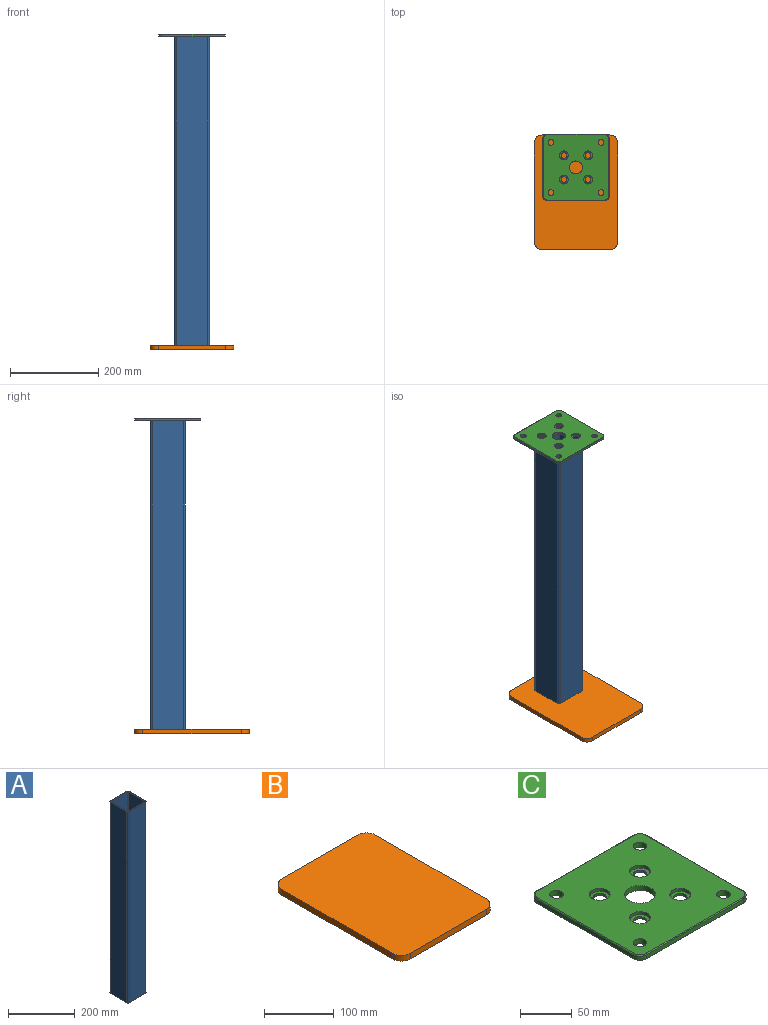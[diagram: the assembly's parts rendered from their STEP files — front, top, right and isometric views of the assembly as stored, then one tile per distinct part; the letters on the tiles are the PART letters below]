
ASSEMBLY  parts=3 mates=2
PART A: 18 faces, bbox 80x80x700 mm
  f0: cylinder r=2mm len=700mm, axis (0,0,-1), area 2199.1mm2, adj f1,f15,f16,f17
  f1: plane 700x70mm, normal (-1,0,0), area 49000mm2, adj f0,f2,f16,f17
  f2: cylinder r=2mm len=700mm, axis (0,0,-1), area 2199.1mm2, adj f1,f3,f16,f17
  f3: plane 700x70mm, normal (0,1,0), area 49000mm2, adj f2,f4,f16,f17
  f4: cylinder r=2mm len=700mm, axis (0,0,-1), area 2199.1mm2, adj f3,f5,f16,f17
  f5: plane 700x70mm, normal (1,0,0), area 49000mm2, adj f4,f6,f16,f17
  f6: cylinder r=2mm len=700mm, axis (0,0,-1), area 2199.1mm2, adj f5,f15,f16,f17
  f7: plane 700x70mm, normal (0,-1,0), area 49000mm2, adj f8,f14,f16,f17
  f8: cylinder r=5mm len=700mm, axis (0,0,-1), area 5497.8mm2, adj f7,f9,f16,f17
  f9: plane 700x70mm, normal (1,0,0), area 49000mm2, adj f8,f10,f16,f17
  f10: cylinder r=5mm len=700mm, axis (0,0,-1), area 5497.8mm2, adj f9,f11,f16,f17
  f11: plane 700x70mm, normal (0,1,0), area 49000mm2, adj f10,f12,f16,f17
  f12: cylinder r=5mm len=700mm, axis (0,0,-1), area 5497.8mm2, adj f11,f13,f16,f17
  f13: plane 700x70mm, normal (-1,0,0), area 49000mm2, adj f12,f14,f16,f17
  f14: cylinder r=5mm len=700mm, axis (0,0,-1), area 5497.8mm2, adj f7,f13,f16,f17
  f15: plane 700x70mm, normal (0,-1,0), area 49000mm2, adj f0,f6,f16,f17
  f16: plane 80x80mm, normal (0,0,1), area 906mm2, adj f0,f1,f2,f3,f4,f5,f6,f7
  f17: plane 80x80mm, normal (0,0,-1), area 906mm2, adj f0,f1,f2,f3,f4,f5,f6,f7
PART B: 10 faces, bbox 190x260x10 mm
  f0: plane 154x10mm, normal (0,-1,0), area 1540mm2, adj f4,f5,f6,f9
  f1: plane 224x10mm, normal (1,0,0), area 2240mm2, adj f4,f5,f6,f7
  f2: plane 154x10mm, normal (0,1,0), area 1540mm2, adj f4,f5,f7,f8
  f3: plane 224x10mm, normal (-1,0,0), area 2240mm2, adj f4,f5,f8,f9
  f4: plane 260x190mm, normal (0,0,1), area 49121.9mm2, adj f0,f1,f2,f3,f6,f7,f8,f9
  f5: plane 260x190mm, normal (0,0,-1), area 49121.9mm2, adj f0,f1,f2,f3,f6,f7,f8,f9
  f6: cylinder r=18mm len=18mm, axis (0,0,-1), area 282.7mm2, adj f0,f1,f4,f5
  f7: cylinder r=18mm len=18mm, axis (0,0,1), area 282.7mm2, adj f1,f2,f4,f5
  f8: cylinder r=18mm len=18mm, axis (0,0,-1), area 282.7mm2, adj f2,f3,f4,f5
  f9: cylinder r=18mm len=18mm, axis (0,0,1), area 282.7mm2, adj f0,f3,f4,f5
PART C: 43 faces, bbox 151.5x151.5x6 mm
  f0: plane 132x4.5mm, normal (-1,0,0), area 594mm2, adj f11,f14,f28,f36
  f1: plane 132x4.5mm, normal (0,-1,0), area 594mm2, adj f11,f12,f32,f37
  f2: plane 132x4.5mm, normal (1,0,0), area 594mm2, adj f12,f13,f33,f41
  f3: cylinder r=14.75mm len=29.5mm, axis (0,0,-1), area 556.1mm2, adj f9,f10
  f4: cylinder r=6.5mm len=13mm, axis (0,0,-1), area 245mm2, adj f9,f10
  f5: cylinder r=6.5mm len=13mm, axis (0,0,-1), area 245mm2, adj f9,f10
  f6: cylinder r=6.5mm len=13mm, axis (0,0,-1), area 245mm2, adj f9,f10
  f7: cylinder r=6.5mm len=13mm, axis (0,0,-1), area 245mm2, adj f9,f10
  f8: plane 132x4.5mm, normal (0,1,0), area 594mm2, adj f13,f14,f29,f40
  f9: plane 148x148mm, normal (0,0,1), area 19378mm2, adj f3,f4,f5,f6,f7,f17,f20,f23
  f10: plane 149x149mm, normal (0,0,-1), area 20393.6mm2, adj f3,f4,f5,f6,f7,f15,f18,f21
  f11: cylinder r=9mm len=9mm, axis (0,0,-1), area 63.6mm2, adj f0,f1,f30,f35
  f12: cylinder r=9mm len=9mm, axis (0,0,1), area 63.6mm2, adj f1,f2,f34,f39
  f13: cylinder r=9mm len=9mm, axis (0,0,-1), area 63.6mm2, adj f2,f8,f31,f42
  f14: cylinder r=9mm len=9mm, axis (0,0,1), area 63.6mm2, adj f0,f8,f27,f38
  f15: cylinder r=6.5mm len=13mm, axis (0,0,1), area 102.1mm2, adj f10,f16
  f16: plane 20x20mm, normal (0,0,1), area 181.4mm2, adj f15,f17
  f17: cylinder r=10mm len=20mm, axis (0,0,1), area 219.9mm2, adj f9,f16
  f18: cylinder r=6.5mm len=13mm, axis (0,0,1), area 102.1mm2, adj f10,f19
  f19: plane 20x20mm, normal (0,0,1), area 181.4mm2, adj f18,f20
  f20: cylinder r=10mm len=20mm, axis (0,0,1), area 219.9mm2, adj f9,f19
  f21: cylinder r=6.5mm len=13mm, axis (0,0,1), area 102.1mm2, adj f10,f22
  f22: plane 20x20mm, normal (0,0,1), area 181.4mm2, adj f21,f23
  f23: cylinder r=10mm len=20mm, axis (0,0,1), area 219.9mm2, adj f9,f22
  f24: cylinder r=6.5mm len=13mm, axis (0,0,1), area 102.1mm2, adj f10,f25
  f25: plane 20x20mm, normal (0,0,1), area 181.4mm2, adj f24,f26
  f26: cylinder r=10mm len=20mm, axis (0,0,1), area 219.9mm2, adj f9,f25
  f27: torus R=8mm, axis (0,0,1), area 21.3mm2, adj f9,f14,f28,f29
  f28: cylinder r=1mm len=132mm, axis (0,1,0), area 207.3mm2, adj f0,f9,f27,f30
  f29: cylinder r=1mm len=132mm, axis (1,0,0), area 207.3mm2, adj f8,f9,f27,f31
  f30: torus R=8mm, axis (0,0,1), area 21.3mm2, adj f9,f11,f28,f32
  f31: torus R=8mm, axis (0,0,1), area 21.3mm2, adj f9,f13,f29,f33
  f32: cylinder r=1mm len=132mm, axis (-1,0,0), area 207.3mm2, adj f1,f9,f30,f34
  f33: cylinder r=1mm len=132mm, axis (0,-1,0), area 207.3mm2, adj f2,f9,f31,f34
  f34: torus R=8mm, axis (0,0,1), area 21.3mm2, adj f9,f12,f32,f33
  f35: torus R=8.5mm, axis (0,0,1), area 10.9mm2, adj f10,f11,f36,f37
  f36: cylinder r=0.5mm len=132mm, axis (0,-1,0), area 103.7mm2, adj f0,f10,f35,f38
  f37: cylinder r=0.5mm len=132mm, axis (1,0,0), area 103.7mm2, adj f1,f10,f35,f39
  f38: torus R=8.5mm, axis (0,0,1), area 10.9mm2, adj f10,f14,f36,f40
  f39: torus R=8.5mm, axis (0,0,1), area 10.9mm2, adj f10,f12,f37,f41
  f40: cylinder r=0.5mm len=132mm, axis (-1,0,0), area 103.7mm2, adj f8,f10,f38,f42
  f41: cylinder r=0.5mm len=132mm, axis (0,1,0), area 103.7mm2, adj f2,f10,f39,f42
  f42: torus R=8.5mm, axis (0,0,1), area 10.9mm2, adj f10,f13,f40,f41
PLACE A t=(-222.68,-6.31,-29.25)mm fixed
PLACE B t=(-222.68,-61.31,-39.25)mm
PLACE C t=(-222.68,-6.31,670.75)mm
MATE fastened A.f17 <-> B.f4  axis (0,0,-1) through (-222.68,-6.31,-29.25)mm
MATE fastened A.f16 <-> C.f3  axis (0,0,1) through (-222.68,-6.31,670.75)mm
